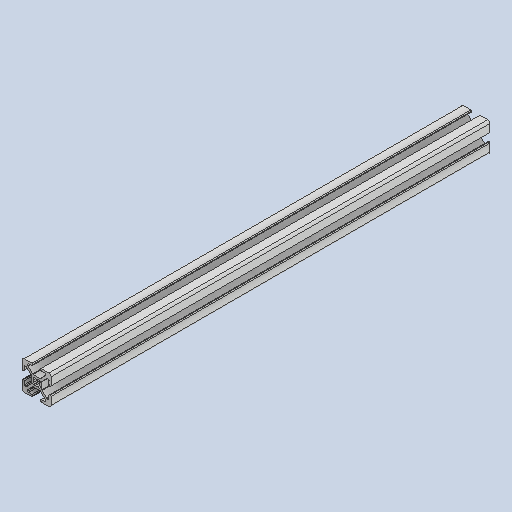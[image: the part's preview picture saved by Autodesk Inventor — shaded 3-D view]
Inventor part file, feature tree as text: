
AUTODESK INVENTOR PART (.ipt)
format: ipt  version: 2022 (Build 260153000, 153)  size: 285,696 bytes
history: native  units: in
note: dims shown in document units (in); Inventor stores cm internally (conversion verified against a paired STEP export)
features: other x3, sketch x1
ambient origin geometry x8: Origin, YZ Plane, XZ Plane, XY Plane, X Axis, Y Axis, Z Axis, Center Point
bodies: Solid1 (feature_tree)
feature tree (4):
  other  "20x20x301.4 T Slot Extrusion Bar.ipt"
  other  "Solid1::20x20x301.4 T Slot Extrusion Bar.ipt"
  other  "TaggingFeature1"
  sketch  "Sketch_1"  dims[d0=0.3937in]
